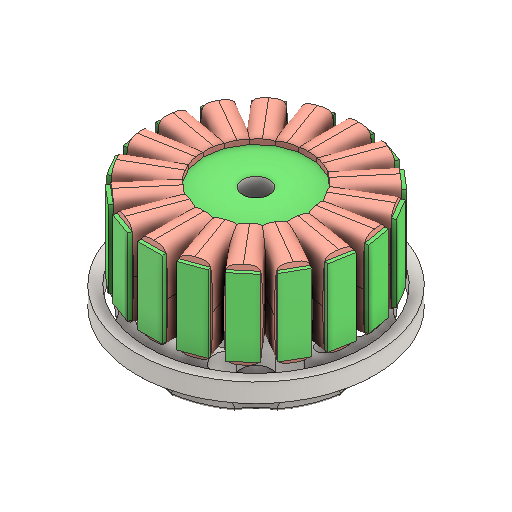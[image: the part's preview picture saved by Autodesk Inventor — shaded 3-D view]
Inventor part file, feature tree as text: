
AUTODESK INVENTOR PART (.ipt)
format: ipt  version: 2022 (Build 260153000, 153)  size: 936,448 bytes
history: mixed  units: in
note: dims shown in document units (in); Inventor stores cm internally (conversion verified against a paired STEP export)
features: fillet x1, imported_body x1
ambient origin geometry x8: Origin, YZ Plane, XZ Plane, XY Plane, X Axis, Y Axis, Z Axis, Center Point
bodies: Solid1 (imported_parasolid)
feature tree (2):
  fillet  "Fillet2"  [1 undecoded]
  imported_body  NMx_Import_Brep_tag  [imported B-rep: ~3 faces, bbox_mm=None]
note: 1 required parameter value undecoded (feature->parameter linkage not recoverable at this tier; creation-order binding heuristic only, values carry confidence <= 0.55)
